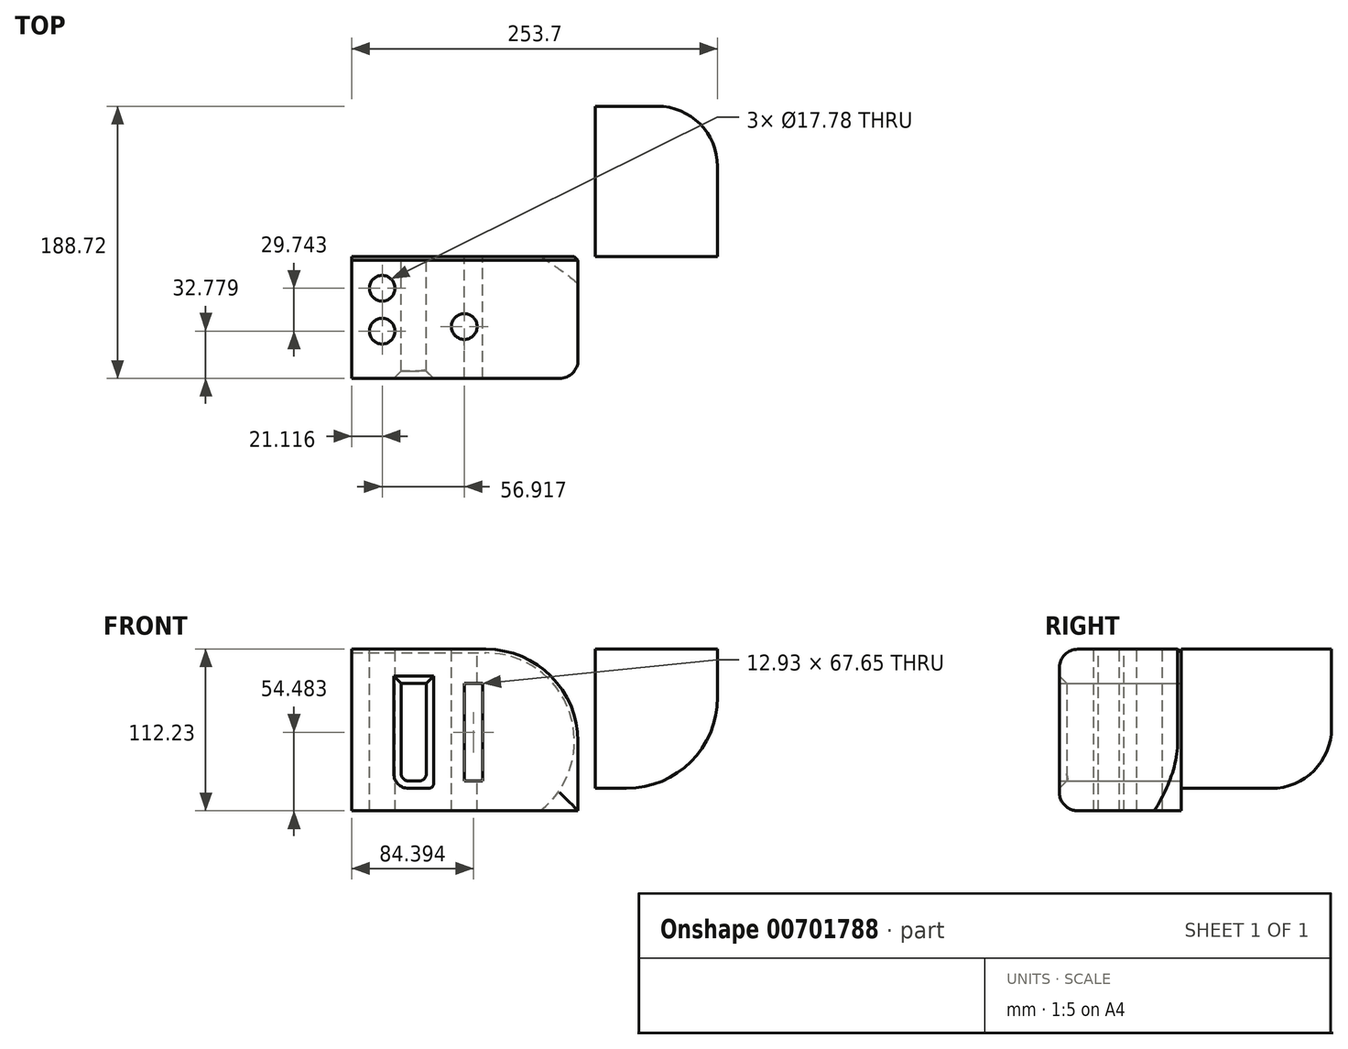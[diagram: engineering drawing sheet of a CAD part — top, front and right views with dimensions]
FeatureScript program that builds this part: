
annotation { "Feature Type Name" : "Feature", "Feature Type Description" : "" }
export const myFeature = defineFeature(function(context is Context, id is Id, definition is map)
    precondition{}
    {
        {
            var Q0;
            Q0=qCreatedBy(makeId("Front.planeOp"),FACE);
            var sketch = newSketch(context, id + "F0", { "sketchPlane" : qUnion([Q0])});
            skLineSegment(sketch, "E0.bottom", {"start": v(-67.27, 47.33) * mm, "end": v(89.64, 47.33) * mm});
            skLineSegment(sketch, "E0.top", {"start": v(-67.27, -64.64) * mm, "end": v(89.64, -64.64) * mm});
            skLineSegment(sketch, "E0.left", {"start": v(-67.27, 47.33) * mm, "end": v(-67.27, -64.64) * mm});
            skLineSegment(sketch, "E0.right", {"start": v(89.64, 47.33) * mm, "end": v(89.64, -64.64) * mm});
            skLineSegment(sketch, "E1.bottom", {"start": v(-33.03, 23.67) * mm, "end": v(-15.55, 23.67) * mm});
            skLineSegment(sketch, "E1.top", {"start": v(-33.03, -43.98) * mm, "end": v(-15.55, -43.98) * mm});
            skLineSegment(sketch, "E1.left", {"start": v(-33.03, 23.67) * mm, "end": v(-33.03, -43.98) * mm});
            skLineSegment(sketch, "E1.right", {"start": v(-15.55, 23.67) * mm, "end": v(-15.55, -43.98) * mm});
            skLineSegment(sketch, "E2.bottom", {"start": v(10.66, 23.67) * mm, "end": v(23.59, 23.67) * mm});
            skLineSegment(sketch, "E2.top", {"start": v(10.66, -43.98) * mm, "end": v(23.59, -43.98) * mm});
            skLineSegment(sketch, "E2.left", {"start": v(10.66, 23.67) * mm, "end": v(10.66, -43.98) * mm});
            skLineSegment(sketch, "E2.right", {"start": v(23.59, 23.67) * mm, "end": v(23.59, -43.98) * mm});
            skSolve(sketch);
        }
        {
            var Q0;
            Q0=makeQuery(id+"F0.imprint","IMPRINT",FACE,{"disambiguationData":[TD([[makeQuery(id+"F0.imprint","IMPRINT",EDGE,{"derivedFrom":sQuery(id+"F0.wireOp",EDGE,"E0.bottom")}),-1.0]])]});
            extrude(context, id + "F1", {"entities" : qUnion([Q0]), "depth" : 84.58 * mm, "offsetDistance" : 25.4 * mm});
        }
        {
            var Q0;
            Q0=makeQuery(id+"F1.opExtrude","SWEPT_EDGE",EDGE,{"disambiguationData":[OSD([sQuery(id+"F0.wireOp",EDGE,"E0.bottom"),sQuery(id+"F0.wireOp",EDGE,"E0.right")])]});
            fillet(context, id + "F2", {"entities" : qUnion([Q0]), "radius" : 63.77 * mm, "tangentPropagation" : true, "allowEdgeOverflow" : false});
        }
        {
            var Q0;
            Q0=makeQuery(id+"F1.opExtrude","CAP_EDGE",EDGE,{"disambiguationData":[OSD([sQuery(id+"F0.wireOp",EDGE,"E0.bottom")])],"isStart":false});
            var Q1;
            Q1=makeQuery(id+"F1.opExtrude","CAP_EDGE",EDGE,{"disambiguationData":[OSD([sQuery(id+"F0.wireOp",EDGE,"E0.top")])],"isStart":false});
            fillet(context, id + "F3", {"entities" : qUnion([Q0, Q1]), "radius" : 12.7 * mm, "tangentPropagation" : true, "allowEdgeOverflow" : false});
        }
        {
            var Q0;
            Q0=makeQuery(id+"F1.opExtrude","SWEPT_FACE",FACE,{"disambiguationData":[OSD([sQuery(id+"F0.wireOp",EDGE,"E0.bottom")])]});
            var sketch = newSketch(context, id + "F4", { "sketchPlane" : qUnion([Q0])});
            skLineSegment(sketch, "E3", {"start": v(-46.15, -22.06) * mm, "end": v(-46.15, -51.8) * mm});
            skPoint(sketch, "E4", {"position": v(7.38, -14.9) * mm});
            skPoint(sketch, "E5", {"position": v(10.76, -48.6) * mm});
            skSolve(sketch);
        }
        {
            var Q0;
            Q0=sQuery(id+"F4.wireOp",VERTEX,"E5");
            var Q1;
            Q1=sQuery(id+"F4.wireOp",VERTEX,"E3.end");
            var Q2;
            Q2=sQuery(id+"F4.wireOp",VERTEX,"E3.start");
            var Q3;
            Q3=makeQuery(id+"F1.opExtrude","SWEPT_BODY",BODY,{"disambiguationData":[OSD([sQuery(id+"F0.wireOp",EDGE,"E0.bottom"),sQuery(id+"F0.wireOp",EDGE,"E0.top"),sQuery(id+"F0.wireOp",EDGE,"E0.left"),sQuery(id+"F0.wireOp",EDGE,"E0.right"),sQuery(id+"F0.wireOp",EDGE,"E1.bottom"),sQuery(id+"F0.wireOp",EDGE,"E1.top"),sQuery(id+"F0.wireOp",EDGE,"E1.left"),sQuery(id+"F0.wireOp",EDGE,"E1.right"),sQuery(id+"F0.wireOp",EDGE,"E2.bottom"),sQuery(id+"F0.wireOp",EDGE,"E2.top"),sQuery(id+"F0.wireOp",EDGE,"E2.left"),sQuery(id+"F0.wireOp",EDGE,"E2.right")])]});
            hole(context, id + "F5", {"style" : HoleStyle.SIMPLE, "endStyle" : HoleEndStyle.THROUGH, "holeDiameter" : 17.78 * mm, "majorDiameter" : 6.35 * mm, "isTappedThrough" : true, "tappedDepth" : 12.7 * mm, "tapClearance" : 3, "locations" : qUnion([Q0, Q1, Q2]), "scope" : qUnion([Q3])});
        }
        {
            var Q0;
            Q0=makeQuery(id+"F1.opExtrude","CAP_EDGE",EDGE,{"disambiguationData":[OSD([sQuery(id+"F0.wireOp",EDGE,"E0.bottom")])],"isStart":true});
            var Q1;
            {var subQ0=sQuery(id+"F0.wireOp",EDGE,"E0.right");var subQ1=sQuery(id+"F0.wireOp",EDGE,"E0.bottom");Q1=makeQuery(id+"F2.opFillet","BLEND_EDGE",EDGE,{"blendedFrom":[makeQuery(id+"F1.opExtrude","SWEPT_EDGE",EDGE,{"disambiguationData":[OSD([subQ1,subQ0])]}),makeQuery(id+"F1.opExtrude","CAP_FACE",FACE,{"disambiguationData":[OSD([subQ1,sQuery(id+"F0.wireOp",EDGE,"E0.top"),sQuery(id+"F0.wireOp",EDGE,"E0.left"),subQ0,sQuery(id+"F0.wireOp",EDGE,"E1.bottom"),sQuery(id+"F0.wireOp",EDGE,"E1.top"),sQuery(id+"F0.wireOp",EDGE,"E1.left"),sQuery(id+"F0.wireOp",EDGE,"E1.right"),sQuery(id+"F0.wireOp",EDGE,"E2.bottom"),sQuery(id+"F0.wireOp",EDGE,"E2.top"),sQuery(id+"F0.wireOp",EDGE,"E2.left"),sQuery(id+"F0.wireOp",EDGE,"E2.right")])],"isStart":true})],"blendedInto":[makeQuery(id+"F1.opExtrude","CAP_FACE",FACE,{"disambiguationData":[OSD([subQ1,sQuery(id+"F0.wireOp",EDGE,"E0.top"),sQuery(id+"F0.wireOp",EDGE,"E0.left"),subQ0,sQuery(id+"F0.wireOp",EDGE,"E1.bottom"),sQuery(id+"F0.wireOp",EDGE,"E1.top"),sQuery(id+"F0.wireOp",EDGE,"E1.left"),sQuery(id+"F0.wireOp",EDGE,"E1.right"),sQuery(id+"F0.wireOp",EDGE,"E2.bottom"),sQuery(id+"F0.wireOp",EDGE,"E2.top"),sQuery(id+"F0.wireOp",EDGE,"E2.left"),sQuery(id+"F0.wireOp",EDGE,"E2.right")])],"isStart":true})]});}
            chamfer(context, id + "F6", {"entities" : qUnion([Q0, Q1]), "width" : 2.54 * mm});
        }
        {
            var Q0;
            Q0=makeQuery(id+"F1.opExtrude","CAP_FACE",FACE,{"disambiguationData":[OSD([sQuery(id+"F0.wireOp",EDGE,"E0.bottom"),sQuery(id+"F0.wireOp",EDGE,"E0.top"),sQuery(id+"F0.wireOp",EDGE,"E0.left"),sQuery(id+"F0.wireOp",EDGE,"E0.right"),sQuery(id+"F0.wireOp",EDGE,"E1.bottom"),sQuery(id+"F0.wireOp",EDGE,"E1.top"),sQuery(id+"F0.wireOp",EDGE,"E1.left"),sQuery(id+"F0.wireOp",EDGE,"E1.right"),sQuery(id+"F0.wireOp",EDGE,"E2.bottom"),sQuery(id+"F0.wireOp",EDGE,"E2.top"),sQuery(id+"F0.wireOp",EDGE,"E2.left"),sQuery(id+"F0.wireOp",EDGE,"E2.right")])],"isStart":true});
            var sketch = newSketch(context, id + "F7", { "sketchPlane" : qUnion([Q0])});
            skLineSegment(sketch, "E6.bottom", {"start": v(-186.43, 47.6) * mm, "end": v(-101.65, 47.6) * mm});
            skLineSegment(sketch, "E6.top", {"start": v(-186.43, -49.12) * mm, "end": v(-101.65, -49.12) * mm});
            skLineSegment(sketch, "E6.left", {"start": v(-186.43, 47.6) * mm, "end": v(-186.43, -49.12) * mm});
            skLineSegment(sketch, "E6.right", {"start": v(-101.65, 47.6) * mm, "end": v(-101.65, -49.12) * mm});
            skSolve(sketch);
        }
        {
            var Q0;
            Q0=makeQuery(id+"F7.imprint","IMPRINT",FACE,{"disambiguationData":[TD([[makeQuery(id+"F7.imprint","IMPRINT",EDGE,{"derivedFrom":sQuery(id+"F7.wireOp",EDGE,"E6.bottom")}),-1.0]])]});
            extrude(context, id + "F8", {"entities" : qUnion([Q0]), "depth" : 104.14 * mm, "offsetDistance" : 25.4 * mm});
        }
        {
            var Q0;
            Q0=makeQuery(id+"F8.opExtrude","SWEPT_EDGE",EDGE,{"disambiguationData":[OSD([sQuery(id+"F7.wireOp",EDGE,"E6.top"),sQuery(id+"F7.wireOp",EDGE,"E6.left")])]});
            fillet(context, id + "F9", {"entities" : qUnion([Q0]), "radius" : 63.16 * mm, "tangentPropagation" : true, "allowEdgeOverflow" : false});
        }
        {
            var Q0;
            Q0=makeQuery(id+"F1.opExtrude","SWEPT_EDGE",EDGE,{"disambiguationData":[OSD([sQuery(id+"F0.wireOp",EDGE,"E1.top"),sQuery(id+"F0.wireOp",EDGE,"E1.left")])]});
            fillet(context, id + "F10", {"entities" : qUnion([Q0]), "radius" : 5.08 * mm, "tangentPropagation" : true, "allowEdgeOverflow" : false});
        }
        {
            var Q0;
            {var subQ0=sQuery(id+"F7.wireOp",EDGE,"E6.left");var subQ1=sQuery(id+"F7.wireOp",EDGE,"E6.top");Q0=makeQuery(id+"F9.opFillet","BLEND_EDGE",EDGE,{"blendedFrom":[makeQuery(id+"F8.opExtrude","SWEPT_EDGE",EDGE,{"disambiguationData":[OSD([subQ1,subQ0])]}),makeQuery(id+"F8.opExtrude","CAP_FACE",FACE,{"disambiguationData":[OSD([sQuery(id+"F7.wireOp",EDGE,"E6.bottom"),subQ1,subQ0,sQuery(id+"F7.wireOp",EDGE,"E6.right")])],"isStart":false})],"blendedInto":[makeQuery(id+"F8.opExtrude","CAP_FACE",FACE,{"disambiguationData":[OSD([sQuery(id+"F7.wireOp",EDGE,"E6.bottom"),subQ1,subQ0,sQuery(id+"F7.wireOp",EDGE,"E6.right")])],"isStart":false})]});}
            fillet(context, id + "F11", {"entities" : qUnion([Q0]), "radius" : 41.7 * mm, "tangentPropagation" : true, "allowEdgeOverflow" : false});
        }
        {
            var Q0;
            Q0=makeQuery(id+"F1.opExtrude","CAP_EDGE",EDGE,{"disambiguationData":[OSD([sQuery(id+"F0.wireOp",EDGE,"E1.left")])],"isStart":false});
            var Q1;
            Q1=makeQuery(id+"F1.opExtrude","CAP_EDGE",EDGE,{"disambiguationData":[OSD([sQuery(id+"F0.wireOp",EDGE,"E1.top")])],"isStart":false});
            var Q2;
            Q2=makeQuery(id+"F1.opExtrude","CAP_EDGE",EDGE,{"disambiguationData":[OSD([sQuery(id+"F0.wireOp",EDGE,"E1.right")])],"isStart":false});
            var Q3;
            Q3=makeQuery(id+"F1.opExtrude","CAP_EDGE",EDGE,{"disambiguationData":[OSD([sQuery(id+"F0.wireOp",EDGE,"E1.bottom")])],"isStart":false});
            chamfer(context, id + "F12", {"entities" : qUnion([Q0, Q1, Q2, Q3]), "width" : 5.08 * mm, "tangentPropagation" : true});
        }
        {
            var Q0;
            Q0=makeQuery(id+"F12.opChamfer","BLEND_EDGE",EDGE,{"blendedFrom":[makeQuery(id+"F1.opExtrude","CAP_EDGE",EDGE,{"disambiguationData":[OSD([sQuery(id+"F0.wireOp",EDGE,"E1.right")])],"isStart":false}),makeQuery(id+"F1.opExtrude","CAP_EDGE",EDGE,{"disambiguationData":[OSD([sQuery(id+"F0.wireOp",EDGE,"E1.top")])],"isStart":false})],"blendedInto":[]});
            fillet(context, id + "F13", {"entities" : qUnion([Q0]), "radius" : 5.08 * mm, "tangentPropagation" : true, "allowEdgeOverflow" : false});
        }
        {
            var Q0;
            Q0=makeQuery(id+"F1.opExtrude","SWEPT_EDGE",EDGE,{"disambiguationData":[OSD([sQuery(id+"F0.wireOp",EDGE,"E1.top"),sQuery(id+"F0.wireOp",EDGE,"E1.right")])]});
            fillet(context, id + "F14", {"entities" : qUnion([Q0]), "radius" : 5.08 * mm, "tangentPropagation" : true, "allowEdgeOverflow" : false});
        }
    });
